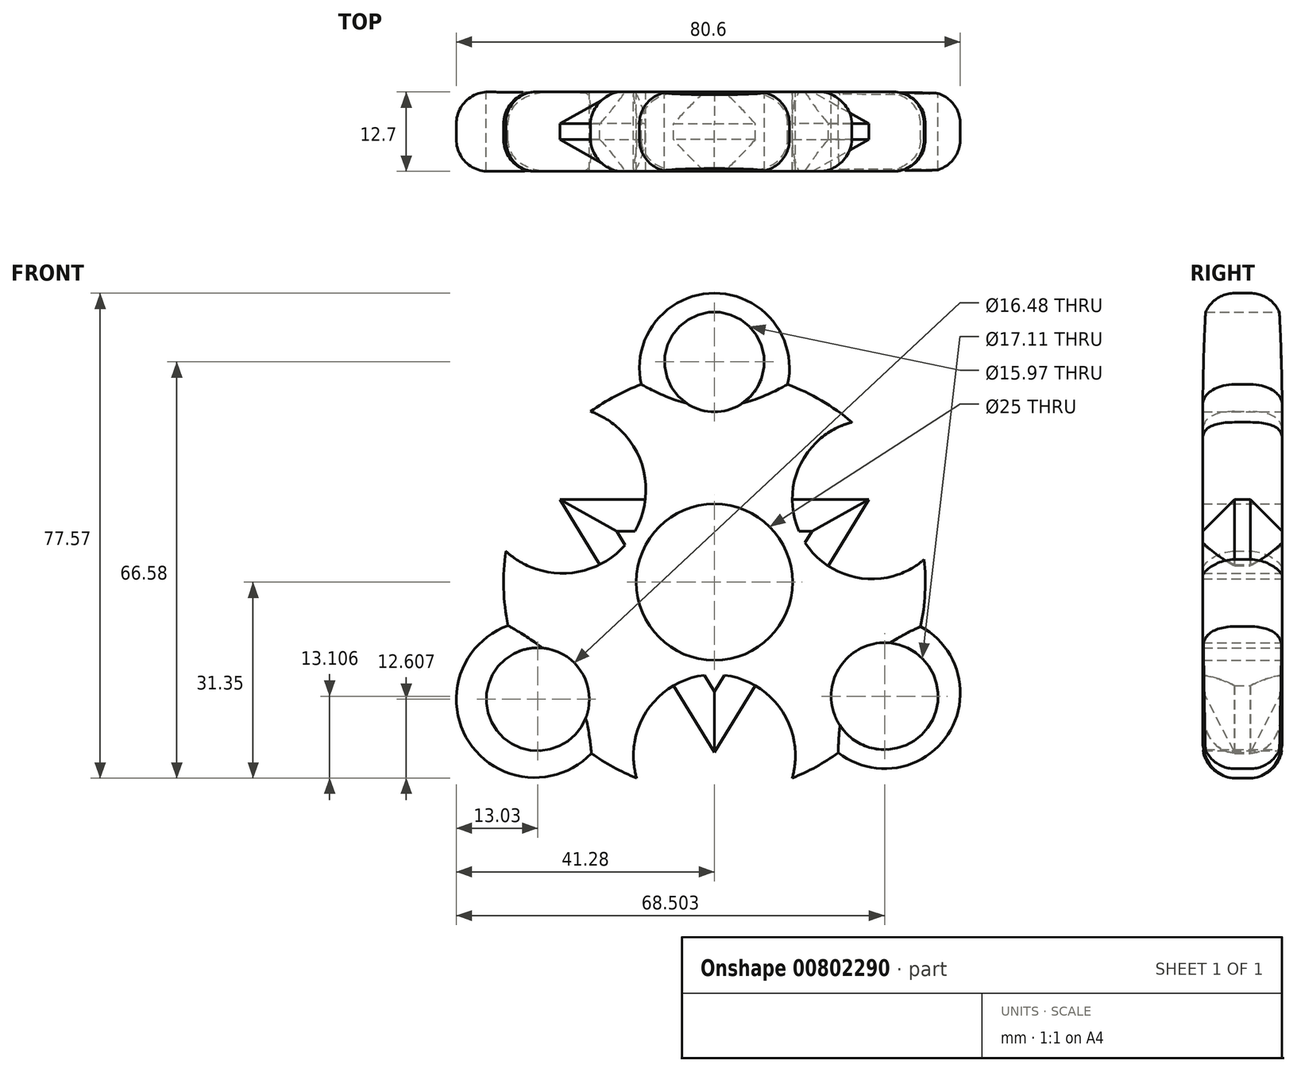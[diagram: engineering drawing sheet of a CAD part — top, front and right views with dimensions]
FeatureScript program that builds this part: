
annotation { "Feature Type Name" : "Feature", "Feature Type Description" : "" }
export const myFeature = defineFeature(function(context is Context, id is Id, definition is map)
    precondition{}
    {
        {
            var Q0;
            Q0=qCreatedBy(makeId("Front.planeOp"),FACE);
            var sketch = newSketch(context, id + "F0", { "sketchPlane" : qUnion([Q0])});
            skCircle(sketch, "E0", {"center": v(0, 0) * mm, "radius": 33.72 * mm});
            skLineSegment(sketch, "E1", {"start": v(-28.98, -17.24) * mm, "end": v(28.98, -17.24) * mm});
            skLineSegment(sketch, "E2", {"start": v(28.98, -17.24) * mm, "end": v(0, 33.72) * mm});
            skLineSegment(sketch, "E3", {"start": v(0, 33.72) * mm, "end": v(-28.98, -17.24) * mm});
            skSolve(sketch);
        }
        {
            var Q0;
            Q0 = qSketchRegion(id + "F0", true);
            extrude(context, id + "F1", {"entities" : qUnion([Q0]), "depth" : 12.7 * mm, "offsetDistance" : 25.4 * mm});
        }
        {
            var Q0;
            Q0=qCreatedBy(makeId("Front.planeOp"),FACE);
            var sketch = newSketch(context, id + "F2", { "sketchPlane" : qUnion([Q0])});
            skCircle(sketch, "E4", {"center": v(0, 34.23) * mm, "radius": 12 * mm});
            skCircle(sketch, "E5", {"center": v(27.22, -17.74) * mm, "radius": 12.1 * mm});
            skCircle(sketch, "E6", {"center": v(-28.75, -18.74) * mm, "radius": 12.53 * mm});
            skSolve(sketch);
        }
        {
            var Q0;
            Q0 = qSketchRegion(id + "F2", true);
            extrude(context, id + "F3", {"entities" : qUnion([Q0]), "operationType" : NewBodyOperationType.ADD, "depth" : 12.7 * mm, "offsetDistance" : 25.4 * mm});
        }
        {
            var Q0;
            Q0=qCreatedBy(makeId("Front.planeOp"),FACE);
            var sketch = newSketch(context, id + "F4", { "sketchPlane" : qUnion([Q0])});
            skCircle(sketch, "E7", {"center": v(0, 35.23) * mm, "radius": 7.99 * mm});
            skCircle(sketch, "E8", {"center": v(27.22, -18.24) * mm, "radius": 8.55 * mm});
            skCircle(sketch, "E9", {"center": v(-28.25, -18.74) * mm, "radius": 8.24 * mm});
            skSolve(sketch);
        }
        {
            var Q0;
            Q0 = qSketchRegion(id + "F4", true);
            extrude(context, id + "F5", {"entities" : qUnion([Q0]), "operationType" : NewBodyOperationType.REMOVE, "endBound" : BoundingType.THROUGH_ALL, "depth" : 25.4 * mm, "offsetDistance" : 25.4 * mm});
        }
        {
            var Q0;
            Q0=qCreatedBy(makeId("Front.planeOp"),FACE);
            var sketch = newSketch(context, id + "F6", { "sketchPlane" : qUnion([Q0])});
            skCircle(sketch, "E10", {"center": v(0, 0) * mm, "radius": 9.27 * mm});
            skSolve(sketch);
        }
        {
            var Q0;
            Q0 = qSketchRegion(id + "F6", true);
            extrude(context, id + "F7", {"entities" : qUnion([Q0]), "operationType" : NewBodyOperationType.REMOVE, "endBound" : BoundingType.THROUGH_ALL, "depth" : 25.4 * mm, "offsetDistance" : 25.4 * mm});
        }
        {
            var Q0;
            {var subQ0=sQuery(id+"F2.wireOp",EDGE,"E4");var subQ1=sQuery(id+"F0.wireOp",EDGE,"E0");var subQ2=sQuery(id+"F2.wireOp",EDGE,"E6");Q0=makeQuery(id+"F3.boolean.opBoolean","SPLIT",EDGE,{"disambiguationData":[TD([makeQuery(id+"F1.opExtrude","SWEPT_FACE",FACE,{"disambiguationData":[OSD([subQ1])]}),makeQuery(id+"F1.opExtrude","CAP_FACE",FACE,{"disambiguationData":[OSD([subQ1])],"isStart":false}),makeQuery(id+"F3.opExtrude","SWEPT_FACE",FACE,{"disambiguationData":[OSD([subQ0])]}),makeQuery(id+"F3.opExtrude","CAP_FACE",FACE,{"disambiguationData":[OSD([subQ0])],"isStart":false}),makeQuery(id+"F3.opExtrude","CAP_FACE",FACE,{"disambiguationData":[OSD([sQuery(id+"F2.wireOp",EDGE,"E5")])],"isStart":false}),makeQuery(id+"F3.opExtrude","SWEPT_FACE",FACE,{"disambiguationData":[OSD([subQ2])]}),makeQuery(id+"F3.opExtrude","CAP_FACE",FACE,{"disambiguationData":[OSD([subQ2])],"isStart":false})])],"derivedFrom":makeQuery(id+"F1.opExtrude","CAP_EDGE",EDGE,{"disambiguationData":[OSD([subQ1])],"isStart":false})});}
            var Q1;
            {var subQ0=sQuery(id+"F2.wireOp",EDGE,"E4");var subQ1=sQuery(id+"F0.wireOp",EDGE,"E0");var subQ2=sQuery(id+"F2.wireOp",EDGE,"E5");Q1=makeQuery(id+"F3.boolean.opBoolean","SPLIT",EDGE,{"disambiguationData":[TD([makeQuery(id+"F1.opExtrude","SWEPT_FACE",FACE,{"disambiguationData":[OSD([subQ1])]}),makeQuery(id+"F1.opExtrude","CAP_FACE",FACE,{"disambiguationData":[OSD([subQ1])],"isStart":false}),makeQuery(id+"F3.opExtrude","SWEPT_FACE",FACE,{"disambiguationData":[OSD([subQ0])]}),makeQuery(id+"F3.opExtrude","CAP_FACE",FACE,{"disambiguationData":[OSD([subQ0])],"isStart":false}),makeQuery(id+"F3.opExtrude","SWEPT_FACE",FACE,{"disambiguationData":[OSD([subQ2])]}),makeQuery(id+"F3.opExtrude","CAP_FACE",FACE,{"disambiguationData":[OSD([subQ2])],"isStart":false}),makeQuery(id+"F3.opExtrude","CAP_FACE",FACE,{"disambiguationData":[OSD([sQuery(id+"F2.wireOp",EDGE,"E6")])],"isStart":false})])],"derivedFrom":makeQuery(id+"F1.opExtrude","CAP_EDGE",EDGE,{"disambiguationData":[OSD([subQ1])],"isStart":false})});}
            var Q2;
            Q2=makeQuery(id+"F3.opExtrude","CAP_EDGE",EDGE,{"disambiguationData":[OSD([sQuery(id+"F2.wireOp",EDGE,"E4")])],"isStart":false});
            var Q3;
            Q3=makeQuery(id+"F3.opExtrude","CAP_EDGE",EDGE,{"disambiguationData":[OSD([sQuery(id+"F2.wireOp",EDGE,"E5")])],"isStart":false});
            var Q4;
            {var subQ0=sQuery(id+"F2.wireOp",EDGE,"E5");var subQ1=sQuery(id+"F0.wireOp",EDGE,"E0");var subQ2=sQuery(id+"F2.wireOp",EDGE,"E6");Q4=makeQuery(id+"F3.boolean.opBoolean","SPLIT",EDGE,{"disambiguationData":[TD([makeQuery(id+"F1.opExtrude","SWEPT_FACE",FACE,{"disambiguationData":[OSD([subQ1])]}),makeQuery(id+"F1.opExtrude","CAP_FACE",FACE,{"disambiguationData":[OSD([subQ1])],"isStart":false}),makeQuery(id+"F3.opExtrude","CAP_FACE",FACE,{"disambiguationData":[OSD([sQuery(id+"F2.wireOp",EDGE,"E4")])],"isStart":false}),makeQuery(id+"F3.opExtrude","SWEPT_FACE",FACE,{"disambiguationData":[OSD([subQ0])]}),makeQuery(id+"F3.opExtrude","CAP_FACE",FACE,{"disambiguationData":[OSD([subQ0])],"isStart":false}),makeQuery(id+"F3.opExtrude","SWEPT_FACE",FACE,{"disambiguationData":[OSD([subQ2])]}),makeQuery(id+"F3.opExtrude","CAP_FACE",FACE,{"disambiguationData":[OSD([subQ2])],"isStart":false})])],"derivedFrom":makeQuery(id+"F1.opExtrude","CAP_EDGE",EDGE,{"disambiguationData":[OSD([subQ1])],"isStart":false})});}
            var Q5;
            Q5=makeQuery(id+"F3.opExtrude","CAP_EDGE",EDGE,{"disambiguationData":[OSD([sQuery(id+"F2.wireOp",EDGE,"E6")])],"isStart":false});
            fillet(context, id + "F8", {"entities" : qUnion([Q0, Q1, Q2, Q3, Q4, Q5]), "radius" : 5.08 * mm, "tangentPropagation" : true, "allowEdgeOverflow" : false});
        }
        {
            var Q0;
            {var subQ0=sQuery(id+"F2.wireOp",EDGE,"E4");var subQ1=sQuery(id+"F0.wireOp",EDGE,"E0");var subQ2=sQuery(id+"F2.wireOp",EDGE,"E6");Q0=makeQuery(id+"F3.boolean.opBoolean","SPLIT",EDGE,{"disambiguationData":[TD([makeQuery(id+"F1.opExtrude","SWEPT_FACE",FACE,{"disambiguationData":[OSD([subQ1])]}),makeQuery(id+"F1.opExtrude","CAP_FACE",FACE,{"disambiguationData":[OSD([subQ1])],"isStart":true}),makeQuery(id+"F3.opExtrude","SWEPT_FACE",FACE,{"disambiguationData":[OSD([subQ0])]}),makeQuery(id+"F3.opExtrude","CAP_FACE",FACE,{"disambiguationData":[OSD([subQ0])],"isStart":true}),makeQuery(id+"F3.opExtrude","CAP_FACE",FACE,{"disambiguationData":[OSD([sQuery(id+"F2.wireOp",EDGE,"E5")])],"isStart":true}),makeQuery(id+"F3.opExtrude","SWEPT_FACE",FACE,{"disambiguationData":[OSD([subQ2])]}),makeQuery(id+"F3.opExtrude","CAP_FACE",FACE,{"disambiguationData":[OSD([subQ2])],"isStart":true})])],"derivedFrom":makeQuery(id+"F1.opExtrude","CAP_EDGE",EDGE,{"disambiguationData":[OSD([subQ1])],"isStart":true})});}
            var Q1;
            Q1=makeQuery(id+"F3.opExtrude","CAP_EDGE",EDGE,{"disambiguationData":[OSD([sQuery(id+"F2.wireOp",EDGE,"E6")])],"isStart":true});
            var Q2;
            {var subQ0=sQuery(id+"F2.wireOp",EDGE,"E5");var subQ1=sQuery(id+"F0.wireOp",EDGE,"E0");var subQ2=sQuery(id+"F2.wireOp",EDGE,"E6");Q2=makeQuery(id+"F3.boolean.opBoolean","SPLIT",EDGE,{"disambiguationData":[TD([makeQuery(id+"F1.opExtrude","SWEPT_FACE",FACE,{"disambiguationData":[OSD([subQ1])]}),makeQuery(id+"F1.opExtrude","CAP_FACE",FACE,{"disambiguationData":[OSD([subQ1])],"isStart":true}),makeQuery(id+"F3.opExtrude","CAP_FACE",FACE,{"disambiguationData":[OSD([sQuery(id+"F2.wireOp",EDGE,"E4")])],"isStart":true}),makeQuery(id+"F3.opExtrude","SWEPT_FACE",FACE,{"disambiguationData":[OSD([subQ0])]}),makeQuery(id+"F3.opExtrude","CAP_FACE",FACE,{"disambiguationData":[OSD([subQ0])],"isStart":true}),makeQuery(id+"F3.opExtrude","SWEPT_FACE",FACE,{"disambiguationData":[OSD([subQ2])]}),makeQuery(id+"F3.opExtrude","CAP_FACE",FACE,{"disambiguationData":[OSD([subQ2])],"isStart":true})])],"derivedFrom":makeQuery(id+"F1.opExtrude","CAP_EDGE",EDGE,{"disambiguationData":[OSD([subQ1])],"isStart":true})});}
            var Q3;
            Q3=makeQuery(id+"F3.opExtrude","CAP_EDGE",EDGE,{"disambiguationData":[OSD([sQuery(id+"F2.wireOp",EDGE,"E5")])],"isStart":true});
            var Q4;
            {var subQ0=sQuery(id+"F2.wireOp",EDGE,"E4");var subQ1=sQuery(id+"F0.wireOp",EDGE,"E0");var subQ2=sQuery(id+"F2.wireOp",EDGE,"E5");Q4=makeQuery(id+"F3.boolean.opBoolean","SPLIT",EDGE,{"disambiguationData":[TD([makeQuery(id+"F1.opExtrude","SWEPT_FACE",FACE,{"disambiguationData":[OSD([subQ1])]}),makeQuery(id+"F1.opExtrude","CAP_FACE",FACE,{"disambiguationData":[OSD([subQ1])],"isStart":true}),makeQuery(id+"F3.opExtrude","SWEPT_FACE",FACE,{"disambiguationData":[OSD([subQ0])]}),makeQuery(id+"F3.opExtrude","CAP_FACE",FACE,{"disambiguationData":[OSD([subQ0])],"isStart":true}),makeQuery(id+"F3.opExtrude","SWEPT_FACE",FACE,{"disambiguationData":[OSD([subQ2])]}),makeQuery(id+"F3.opExtrude","CAP_FACE",FACE,{"disambiguationData":[OSD([subQ2])],"isStart":true}),makeQuery(id+"F3.opExtrude","CAP_FACE",FACE,{"disambiguationData":[OSD([sQuery(id+"F2.wireOp",EDGE,"E6")])],"isStart":true})])],"derivedFrom":makeQuery(id+"F1.opExtrude","CAP_EDGE",EDGE,{"disambiguationData":[OSD([subQ1])],"isStart":true})});}
            var Q5;
            Q5=makeQuery(id+"F3.opExtrude","CAP_EDGE",EDGE,{"disambiguationData":[OSD([sQuery(id+"F2.wireOp",EDGE,"E4")])],"isStart":true});
            fillet(context, id + "F9", {"entities" : qUnion([Q0, Q1, Q2, Q3, Q4, Q5]), "radius" : 5.08 * mm, "tangentPropagation" : true, "allowEdgeOverflow" : false});
        }
        {
            var Q0;
            Q0=qCreatedBy(makeId("Front.planeOp"),FACE);
            var sketch = newSketch(context, id + "F10", { "sketchPlane" : qUnion([Q0])});
            skLineSegment(sketch, "E11", {"start": v(0, -27.24) * mm, "end": v(24.68, 13.24) * mm});
            skLineSegment(sketch, "E12", {"start": v(24.68, 13.24) * mm, "end": v(-24.68, 13.24) * mm});
            skLineSegment(sketch, "E13", {"start": v(-24.68, 13.24) * mm, "end": v(0, -27.24) * mm});
            skSolve(sketch);
        }
        {
            var Q0;
            Q0=qCreatedBy(makeId("Front.planeOp"),FACE);
            var sketch = newSketch(context, id + "F11", { "sketchPlane" : qUnion([Q0])});
            skCircle(sketch, "E14", {"center": v(25.18, 13.24) * mm, "radius": 12.74 * mm});
            skCircle(sketch, "E15", {"center": v(-24.3, 14.74) * mm, "radius": 13.34 * mm});
            skCircle(sketch, "E16", {"center": v(0, -27.74) * mm, "radius": 12.95 * mm});
            skSolve(sketch);
        }
        {
            var Q0;
            Q0 = qSketchRegion(id + "F11", true);
            extrude(context, id + "F12", {"entities" : qUnion([Q0]), "operationType" : NewBodyOperationType.REMOVE, "endBound" : BoundingType.THROUGH_ALL, "depth" : 25.4 * mm, "offsetDistance" : 25.4 * mm});
        }
        {
            var Q0;
            Q0=makeQuery(id+"F10.imprint","IMPRINT",FACE,{"disambiguationData":[TD([[makeQuery(id+"F10.imprint","IMPRINT",EDGE,{"derivedFrom":sQuery(id+"F10.wireOp",EDGE,"E11")}),1.0]])]});
            extrude(context, id + "F13", {"entities" : qUnion([Q0]), "operationType" : NewBodyOperationType.ADD, "depth" : 12.7 * mm, "offsetDistance" : 25.4 * mm});
        }
        {
            var Q0;
            {var subQ0=sQuery(id+"F10.wireOp",EDGE,"E12");Q0=makeQuery(id+"F13.boolean.opBoolean","SPLIT",EDGE,{"disambiguationData":[TD([makeQuery(id+"F12.boolean.opBoolean","COPY",FACE,{"derivedFrom":makeQuery(id+"F12.opExtrude","SWEPT_FACE",FACE,{"disambiguationData":[OSD([sQuery(id+"F11.wireOp",EDGE,"E14")])]})})])],"derivedFrom":makeQuery(id+"F13.opExtrude","CAP_EDGE",EDGE,{"disambiguationData":[OSD([subQ0])],"isStart":false})});}
            var Q1;
            {var subQ1=sQuery(id+"F10.wireOp",EDGE,"E11");Q1=makeQuery(id+"F13.boolean.opBoolean","SPLIT",EDGE,{"disambiguationData":[TD([makeQuery(id+"F12.boolean.opBoolean","COPY",FACE,{"derivedFrom":makeQuery(id+"F12.opExtrude","SWEPT_FACE",FACE,{"disambiguationData":[OSD([sQuery(id+"F11.wireOp",EDGE,"E14")])]})})])],"derivedFrom":makeQuery(id+"F13.opExtrude","CAP_EDGE",EDGE,{"disambiguationData":[OSD([subQ1])],"isStart":false})});}
            var Q2;
            {var subQ0=sQuery(id+"F10.wireOp",EDGE,"E11");Q2=makeQuery(id+"F13.boolean.opBoolean","SPLIT",EDGE,{"disambiguationData":[TD([makeQuery(id+"F12.boolean.opBoolean","COPY",FACE,{"derivedFrom":makeQuery(id+"F12.opExtrude","SWEPT_FACE",FACE,{"disambiguationData":[OSD([sQuery(id+"F11.wireOp",EDGE,"E16")])]})})])],"derivedFrom":makeQuery(id+"F13.opExtrude","CAP_EDGE",EDGE,{"disambiguationData":[OSD([subQ0])],"isStart":false})});}
            var Q3;
            {var subQ0=sQuery(id+"F10.wireOp",EDGE,"E13");Q3=makeQuery(id+"F13.boolean.opBoolean","SPLIT",EDGE,{"disambiguationData":[TD([makeQuery(id+"F12.boolean.opBoolean","COPY",FACE,{"derivedFrom":makeQuery(id+"F12.opExtrude","SWEPT_FACE",FACE,{"disambiguationData":[OSD([sQuery(id+"F11.wireOp",EDGE,"E16")])]})})])],"derivedFrom":makeQuery(id+"F13.opExtrude","CAP_EDGE",EDGE,{"disambiguationData":[OSD([subQ0])],"isStart":true})});}
            var Q4;
            {var subQ1=sQuery(id+"F10.wireOp",EDGE,"E13");Q4=makeQuery(id+"F13.boolean.opBoolean","SPLIT",EDGE,{"disambiguationData":[TD([makeQuery(id+"F12.boolean.opBoolean","COPY",FACE,{"derivedFrom":makeQuery(id+"F12.opExtrude","SWEPT_FACE",FACE,{"disambiguationData":[OSD([sQuery(id+"F11.wireOp",EDGE,"E15")])]})})])],"derivedFrom":makeQuery(id+"F13.opExtrude","CAP_EDGE",EDGE,{"disambiguationData":[OSD([subQ1])],"isStart":false})});}
            var Q5;
            {var subQ0=sQuery(id+"F10.wireOp",EDGE,"E12");Q5=makeQuery(id+"F13.boolean.opBoolean","SPLIT",EDGE,{"disambiguationData":[TD([makeQuery(id+"F12.boolean.opBoolean","COPY",FACE,{"derivedFrom":makeQuery(id+"F12.opExtrude","SWEPT_FACE",FACE,{"disambiguationData":[OSD([sQuery(id+"F11.wireOp",EDGE,"E15")])]})})])],"derivedFrom":makeQuery(id+"F13.opExtrude","CAP_EDGE",EDGE,{"disambiguationData":[OSD([subQ0])],"isStart":false})});}
            var Q6;
            {var subQ1=sQuery(id+"F10.wireOp",EDGE,"E13");Q6=makeQuery(id+"F13.boolean.opBoolean","SPLIT",EDGE,{"disambiguationData":[TD([makeQuery(id+"F12.boolean.opBoolean","COPY",FACE,{"derivedFrom":makeQuery(id+"F12.opExtrude","SWEPT_FACE",FACE,{"disambiguationData":[OSD([sQuery(id+"F11.wireOp",EDGE,"E16")])]})})])],"derivedFrom":makeQuery(id+"F13.opExtrude","CAP_EDGE",EDGE,{"disambiguationData":[OSD([subQ1])],"isStart":false})});}
            chamfer(context, id + "F14", {"entities" : qUnion([Q0, Q1, Q2, Q3, Q4, Q5, Q6]), "width" : 5.08 * mm, "tangentPropagation" : true});
        }
        {
            var Q0;
            {var subQ1=sQuery(id+"F10.wireOp",EDGE,"E12");Q0=makeQuery(id+"F13.boolean.opBoolean","SPLIT",EDGE,{"disambiguationData":[TD([makeQuery(id+"F12.boolean.opBoolean","COPY",FACE,{"derivedFrom":makeQuery(id+"F12.opExtrude","SWEPT_FACE",FACE,{"disambiguationData":[OSD([sQuery(id+"F11.wireOp",EDGE,"E15")])]})})])],"derivedFrom":makeQuery(id+"F13.opExtrude","CAP_EDGE",EDGE,{"disambiguationData":[OSD([subQ1])],"isStart":true})});}
            var Q1;
            {var subQ1=sQuery(id+"F10.wireOp",EDGE,"E12");Q1=makeQuery(id+"F13.boolean.opBoolean","SPLIT",EDGE,{"disambiguationData":[TD([makeQuery(id+"F12.boolean.opBoolean","COPY",FACE,{"derivedFrom":makeQuery(id+"F12.opExtrude","SWEPT_FACE",FACE,{"disambiguationData":[OSD([sQuery(id+"F11.wireOp",EDGE,"E14")])]})})])],"derivedFrom":makeQuery(id+"F13.opExtrude","CAP_EDGE",EDGE,{"disambiguationData":[OSD([subQ1])],"isStart":true})});}
            var Q2;
            {var subQ0=sQuery(id+"F10.wireOp",EDGE,"E11");Q2=makeQuery(id+"F13.boolean.opBoolean","SPLIT",EDGE,{"disambiguationData":[TD([makeQuery(id+"F12.boolean.opBoolean","COPY",FACE,{"derivedFrom":makeQuery(id+"F12.opExtrude","SWEPT_FACE",FACE,{"disambiguationData":[OSD([sQuery(id+"F11.wireOp",EDGE,"E14")])]})})])],"derivedFrom":makeQuery(id+"F13.opExtrude","CAP_EDGE",EDGE,{"disambiguationData":[OSD([subQ0])],"isStart":true})});}
            var Q3;
            {var subQ1=sQuery(id+"F10.wireOp",EDGE,"E11");Q3=makeQuery(id+"F13.boolean.opBoolean","SPLIT",EDGE,{"disambiguationData":[TD([makeQuery(id+"F12.boolean.opBoolean","COPY",FACE,{"derivedFrom":makeQuery(id+"F12.opExtrude","SWEPT_FACE",FACE,{"disambiguationData":[OSD([sQuery(id+"F11.wireOp",EDGE,"E16")])]})})])],"derivedFrom":makeQuery(id+"F13.opExtrude","CAP_EDGE",EDGE,{"disambiguationData":[OSD([subQ1])],"isStart":true})});}
            var Q4;
            {var subQ0=sQuery(id+"F10.wireOp",EDGE,"E13");Q4=makeQuery(id+"F13.boolean.opBoolean","SPLIT",EDGE,{"disambiguationData":[TD([makeQuery(id+"F12.boolean.opBoolean","COPY",FACE,{"derivedFrom":makeQuery(id+"F12.opExtrude","SWEPT_FACE",FACE,{"disambiguationData":[OSD([sQuery(id+"F11.wireOp",EDGE,"E15")])]})})])],"derivedFrom":makeQuery(id+"F13.opExtrude","CAP_EDGE",EDGE,{"disambiguationData":[OSD([subQ0])],"isStart":true})});}
            chamfer(context, id + "F15", {"entities" : qUnion([Q0, Q1, Q2, Q3, Q4]), "width" : 5.08 * mm, "tangentPropagation" : true});
        }
        {
            var Q0;
            Q0=qCreatedBy(makeId("Front.planeOp"),FACE);
            var sketch = newSketch(context, id + "F16", { "sketchPlane" : qUnion([Q0])});
            skCircle(sketch, "E17", {"center": v(0, 0) * mm, "radius": 12.5 * mm});
            skSolve(sketch);
        }
        {
            var Q0;
            Q0 = qSketchRegion(id + "F16", true);
            extrude(context, id + "F17", {"entities" : qUnion([Q0]), "operationType" : NewBodyOperationType.REMOVE, "endBound" : BoundingType.THROUGH_ALL, "depth" : 25 * mm, "offsetDistance" : 25 * mm});
        }
    });
